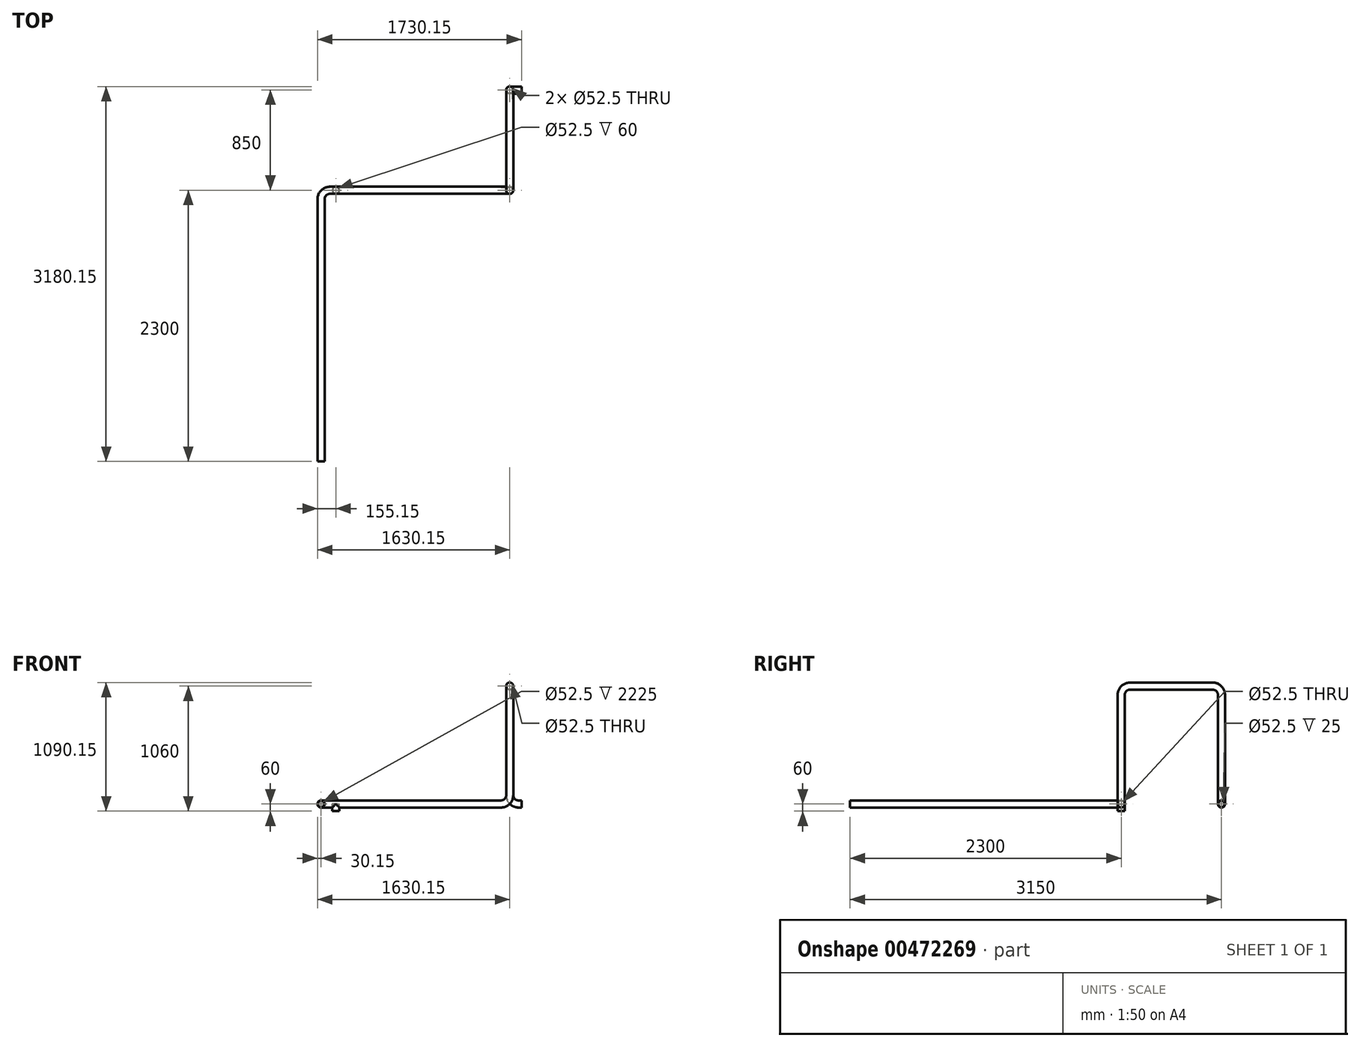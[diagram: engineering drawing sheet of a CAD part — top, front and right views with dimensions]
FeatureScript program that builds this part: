
annotation { "Feature Type Name" : "Feature", "Feature Type Description" : "" }
export const myFeature = defineFeature(function(context is Context, id is Id, definition is map)
    precondition{}
    {
        {
            var Q0;
            Q0=qCreatedBy(makeId("Right.planeOp"),FACE);
            var sketch = newSketch(context, id + "F0", { "sketchPlane" : qUnion([Q0])});
            skLineSegment(sketch, "E0", {"start": v(0, 0) * mm, "end": v(0, 925) * mm});
            skLineSegment(sketch, "E1", {"start": v(-75, 1000) * mm, "end": v(-775, 1000) * mm});
            skLineSegment(sketch, "E2", {"start": v(-850, 925) * mm, "end": v(-850, 0) * mm});
            skPoint(sketch, "E3.visualSharp", {"position": v(0, 1000) * mm});
            skArc(sketch, "E3.filletArc", {"start": v(0, 925) * mm, "mid": v(-21.97, 978.03) * mm, "end": v(-75, 1000) * mm});
            skPoint(sketch, "E4.visualSharp", {"position": v(-850, 1000) * mm});
            skArc(sketch, "E4.filletArc", {"start": v(-775, 1000) * mm, "mid": v(-828.03, 978.03) * mm, "end": v(-850, 925) * mm});
            skSolve(sketch);
        }
        {
            var Q0;
            Q0=qCreatedBy(makeId("Front.planeOp"),FACE);
            var Q1;
            Q1=sQuery(id+"F0.wireOp",VERTEX,"E2.end");
            cPlane(context, id + "F1", {"entities" : qUnion([Q0, Q1]), "cplaneType" : CPlaneType.PLANE_POINT, "offset" : 25 * mm, "width" : 150 * mm, "height" : 150 * mm});
        }
        {
            var Q0;
            Q0=qCreatedBy(id+"F1.planeOp",FACE);
            var sketch = newSketch(context, id + "F2", { "sketchPlane" : qUnion([Q0])});
            skLineSegment(sketch, "E5.0", {"start": v(0, 925) * mm, "end": v(0, 75) * mm});
            skLineSegment(sketch, "E6", {"start": v(-75, 0) * mm, "end": v(-1600, 0) * mm});
            skPoint(sketch, "E7.visualSharp", {"position": v(0, 0) * mm});
            skArc(sketch, "E7.filletArc", {"start": v(-75, 0) * mm, "mid": v(-21.97, 21.97) * mm, "end": v(0, 75) * mm});
            skSolve(sketch);
        }
        {
            var Q0;
            Q0=qCreatedBy(makeId("Top.planeOp"),FACE);
            var sketch = newSketch(context, id + "F3", { "sketchPlane" : qUnion([Q0])});
            skLineSegment(sketch, "E8.0", {"start": v(-75, -850) * mm, "end": v(-1525, -850) * mm});
            skLineSegment(sketch, "E9", {"start": v(-1600, -925) * mm, "end": v(-1600, -3150) * mm});
            skPoint(sketch, "E10.visualSharp", {"position": v(-1600, -850) * mm});
            skArc(sketch, "E10.filletArc", {"start": v(-1525, -850) * mm, "mid": v(-1578.03, -871.97) * mm, "end": v(-1600, -925) * mm});
            skSolve(sketch);
        }
        {
            var Q0;
            Q0=qCreatedBy(makeId("Front.planeOp"),FACE);
            var sketch = newSketch(context, id + "F4", { "sketchPlane" : qUnion([Q0])});
            skLineSegment(sketch, "E11.0", {"start": v(0, 75) * mm, "end": v(0, 925) * mm});
            skLineSegment(sketch, "E12", {"start": v(75, 0) * mm, "end": v(100, 0) * mm});
            skPoint(sketch, "E13.visualSharp", {"position": v(0, 0) * mm});
            skArc(sketch, "E13.filletArc", {"start": v(0, 75) * mm, "mid": v(21.97, 21.97) * mm, "end": v(75, 0) * mm});
            skSolve(sketch);
        }
        {
            var Q0;
            Q0=qCreatedBy(makeId("Right.planeOp"),FACE);
            var Q1;
            Q1=sQuery(id+"F4.wireOp",VERTEX,"E12.end");
            cPlane(context, id + "F5", {"entities" : qUnion([Q0, Q1]), "cplaneType" : CPlaneType.PLANE_POINT, "offset" : 25 * mm, "width" : 150 * mm, "height" : 150 * mm});
        }
        {
            var Q0;
            Q0=qCreatedBy(id+"F5.planeOp",FACE);
            var sketch = newSketch(context, id + "F6", { "sketchPlane" : qUnion([Q0])});
            skCircle(sketch, "E14", {"center": v(0, 0) * mm, "radius": 30.15 * mm});
            skCircle(sketch, "E15", {"center": v(0, 0) * mm, "radius": 26.25 * mm});
            skSolve(sketch);
        }
        {
            var Q0;
            Q0=makeQuery(id+"F6.imprint","IMPRINT",FACE,{"disambiguationData":[TD([[makeQuery(id+"F6.imprint","IMPRINT",EDGE,{"derivedFrom":sQuery(id+"F6.wireOp",EDGE,"E14")}),1.0]])]});
            var Q1;
            Q1=sQuery(id+"F4.wireOp",EDGE,"E12");
            var Q2;
            Q2=sQuery(id+"F4.wireOp",EDGE,"E13.filletArc");
            var Q3;
            Q3=sQuery(id+"F4.wireOp",EDGE,"E11.0");
            var Q4;
            Q4=sQuery(id+"F0.wireOp",EDGE,"E3.filletArc");
            var Q5;
            Q5=sQuery(id+"F0.wireOp",EDGE,"E1");
            var Q6;
            Q6=sQuery(id+"F0.wireOp",EDGE,"E4.filletArc");
            var Q7;
            Q7=sQuery(id+"F2.wireOp",EDGE,"E5.0");
            var Q8;
            Q8=sQuery(id+"F2.wireOp",EDGE,"E7.filletArc");
            var Q9;
            Q9=sQuery(id+"F3.wireOp",EDGE,"E8.0");
            var Q10;
            Q10=sQuery(id+"F3.wireOp",EDGE,"E10.filletArc");
            var Q11;
            Q11=sQuery(id+"F3.wireOp",EDGE,"E9");
            sweep(context, id + "F7", {"profiles" : qUnion([Q0]), "path" : qUnion([Q1, Q2, Q3, Q4, Q5, Q6, Q7, Q8, Q9, Q10, Q11])});
        }
        {
            var Q0;
            Q0=qCreatedBy(makeId("Top.planeOp"),FACE);
            var sketch = newSketch(context, id + "F8", { "sketchPlane" : qUnion([Q0])});
            skLineSegment(sketch, "E16", {"start": v(-75, -880.15) * mm, "end": v(-1525, -880.15) * mm});
            skLineSegment(sketch, "E17", {"start": v(-1525, -819.85) * mm, "end": v(-75, -819.85) * mm});
            skCircle(sketch, "E18", {"center": v(-1475, -850) * mm, "radius": 30.15 * mm});
            skCircle(sketch, "E19", {"center": v(-1475, -850) * mm, "radius": 26.25 * mm});
            skSolve(sketch);
        }
        {
            var Q0;
            Q0 = qSketchRegion(id + "F8", true);
            extrude(context, id + "F9", {"entities" : qUnion([Q0]), "operationType" : NewBodyOperationType.ADD, "oppositeDirection" : true, "depth" : 60 * mm});
        }
        {
            var Q0;
            Q0=makeQuery(id+"F9.opExtrude","CAP_FACE",FACE,{"disambiguationData":[OSD([sQuery(id+"F8.wireOp",EDGE,"E18"),sQuery(id+"F8.wireOp",EDGE,"E19")])],"isStart":false});
            var sketch = newSketch(context, id + "F10", { "sketchPlane" : qUnion([Q0])});
            skCircle(sketch, "E20.0", {"center": v(-1475, 850) * mm, "radius": 26.25 * mm});
            skSolve(sketch);
        }
        {
            var Q0;
            Q0=makeQuery(id+"F10.imprint","IMPRINT",FACE,{"disambiguationData":[TD([[makeQuery(id+"F10.imprint","IMPRINT",EDGE,{"derivedFrom":sQuery(id+"F10.wireOp",EDGE,"E20.0")}),-1.0]])]});
            extrude(context, id + "F11", {"entities" : qUnion([Q0]), "operationType" : NewBodyOperationType.REMOVE, "oppositeDirection" : true, "depth" : 60 * mm});
        }
    });
